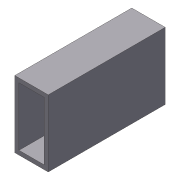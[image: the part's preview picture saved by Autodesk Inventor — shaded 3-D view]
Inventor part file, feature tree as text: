
AUTODESK INVENTOR PART (.ipt)
format: ipt  version: 2012 (Build 160160000, 160)  size: 72,192 bytes
history: native  units: in
note: dims shown in document units (in); Inventor stores cm internally (conversion verified against a paired STEP export)
features: extrude x1, shell x1, sketch x1
ambient origin geometry x8: Origin, YZ Plane, XZ Plane, XY Plane, X Axis, Y Axis, Z Axis, Center Point
bodies: Solid1 (feature_tree)
feature tree (3):
  extrude  "Extrusion1"  Depth=2.0in
  shell  "Shell1"  Thickness=3.5in
  sketch  "Sketch1"  dims[d0=1.0in d1=2.0in d2=3.5in d3=0.0in d4=0.125in]
